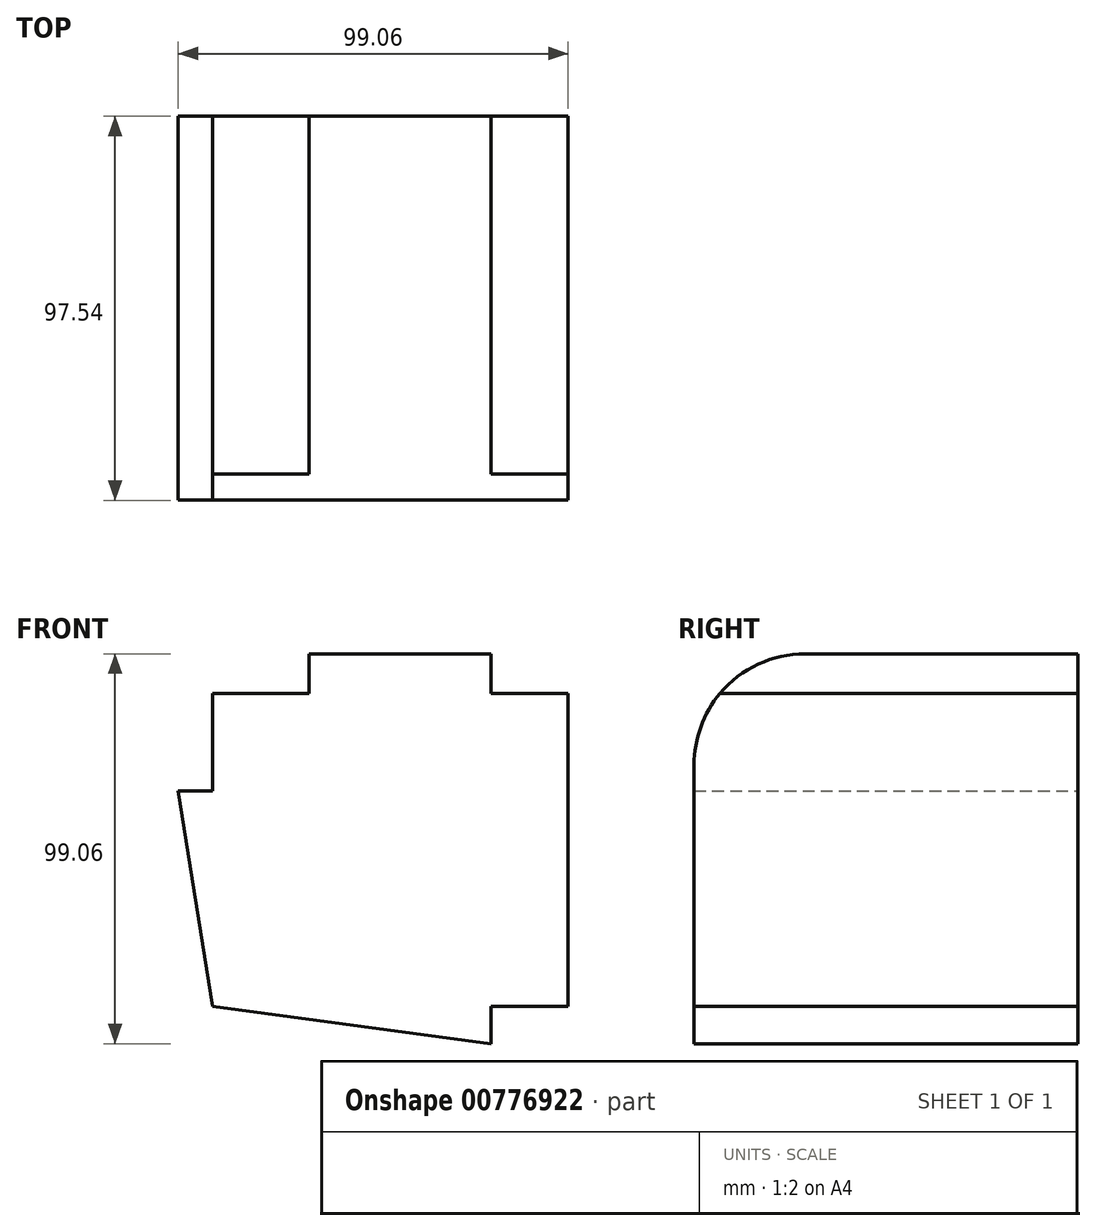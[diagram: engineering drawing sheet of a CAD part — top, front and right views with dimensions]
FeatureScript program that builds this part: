
annotation { "Feature Type Name" : "Feature", "Feature Type Description" : "" }
export const myFeature = defineFeature(function(context is Context, id is Id, definition is map)
    precondition{}
    {
        {
            var Q0;
            Q0=qCreatedBy(makeId("Front.planeOp"),FACE);
            var sketch = newSketch(context, id + "F0", { "sketchPlane" : qUnion([Q0])});
            skLineSegment(sketch, "E0.bottom", {"start": v(-45.04, 40.69) * mm, "end": v(-20.55, 40.69) * mm});
            skLineSegment(sketch, "E0.top", {"start": v(25.72, -38.78) * mm, "end": v(45.31, -38.78) * mm});
            skLineSegment(sketch, "E0.left", {"start": v(-45.04, 40.69) * mm, "end": v(-45.04, 15.92) * mm});
            skLineSegment(sketch, "E0.right", {"start": v(45.31, 40.69) * mm, "end": v(45.31, -38.78) * mm});
            skLineSegment(sketch, "E1", {"start": v(-53.75, 15.92) * mm, "end": v(-45.04, 15.92) * mm});
            skLineSegment(sketch, "E2", {"start": v(-20.55, 40.69) * mm, "end": v(-20.55, 50.75) * mm});
            skLineSegment(sketch, "E3", {"start": v(-20.55, 50.75) * mm, "end": v(25.72, 50.75) * mm});
            skLineSegment(sketch, "E4", {"start": v(25.72, 50.75) * mm, "end": v(25.72, 40.69) * mm});
            skLineSegment(sketch, "E5", {"start": v(25.72, -48.3) * mm, "end": v(-45.04, -38.78) * mm});
            skLineSegment(sketch, "E6", {"start": v(-53.75, 15.92) * mm, "end": v(-45.04, -38.78) * mm});
            skLineSegment(sketch, "E7.trimOffspring", {"start": v(25.72, 40.69) * mm, "end": v(45.31, 40.69) * mm});
            skLineSegment(sketch, "E8.trimOffspring", {"start": v(25.72, -38.78) * mm, "end": v(25.72, -48.3) * mm});
            skSolve(sketch);
        }
        {
            var Q0;
            Q0 = qSketchRegion(id + "F0", true);
            extrude(context, id + "F1", {"entities" : qUnion([Q0]), "depth" : 97.54 * mm, "offsetDistance" : 25.4 * mm});
        }
        {
            var Q0;
            Q0=makeQuery(id+"F1.opExtrude","CAP_EDGE",EDGE,{"disambiguationData":[OSD([sQuery(id+"F0.wireOp",EDGE,"E3")])],"isStart":false});
            fillet(context, id + "F2", {"entities" : qUnion([Q0]), "radius" : 28.2 * mm, "tangentPropagation" : true, "allowEdgeOverflow" : false});
        }
    });
